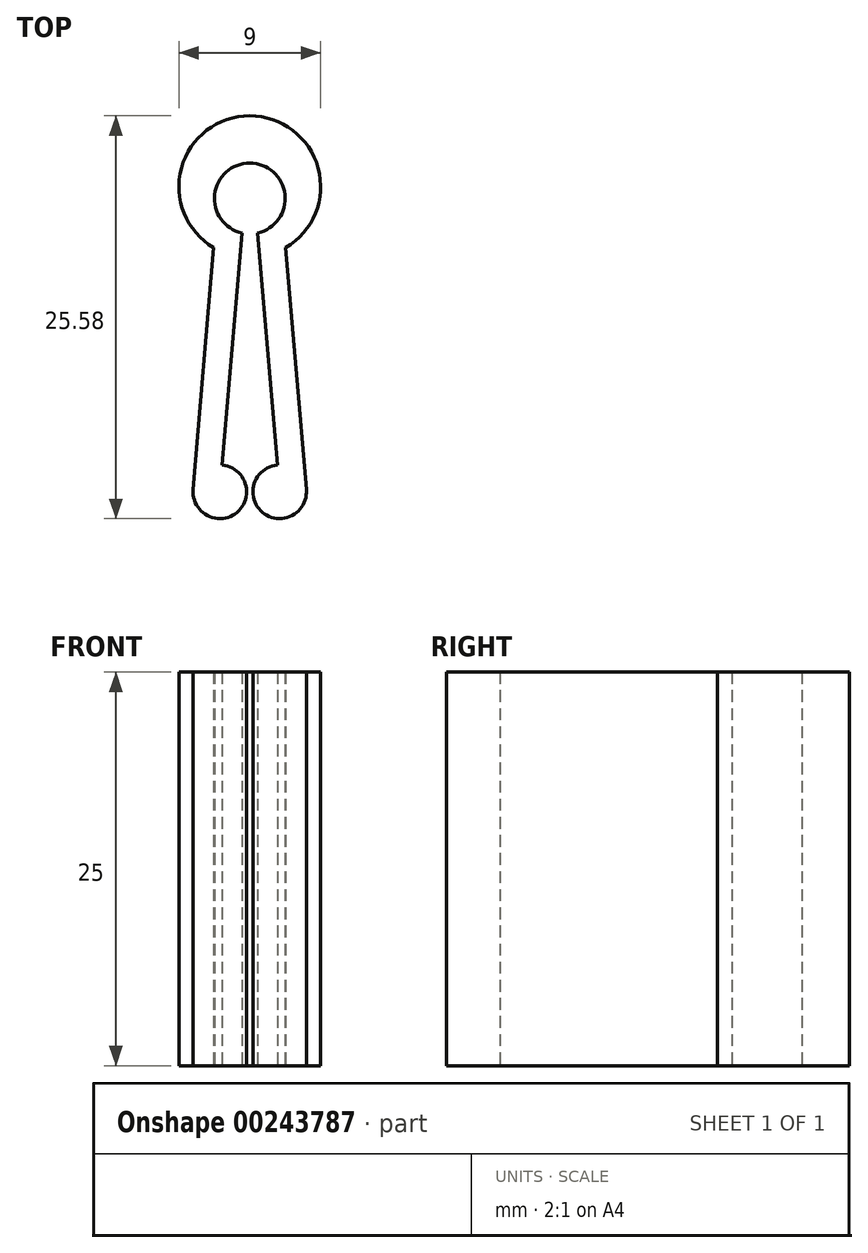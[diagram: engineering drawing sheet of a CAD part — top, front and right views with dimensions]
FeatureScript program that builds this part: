
annotation { "Feature Type Name" : "Feature", "Feature Type Description" : "" }
export const myFeature = defineFeature(function(context is Context, id is Id, definition is map)
    precondition{}
    {
        {
            var Q0;
            Q0=qCreatedBy(makeId("Top.planeOp"),FACE);
            var sketch = newSketch(context, id + "F0", { "sketchPlane" : qUnion([Q0])});
            skArc(sketch, "E0", {"start": v(0.5, 18) * mm, "mid": v(0, 22.44) * mm, "end": v(-0.5, 18) * mm});
            skLineSegment(sketch, "E1", {"start": v(0.5, 18) * mm, "end": v(1.76, 3.25) * mm});
            skLineSegment(sketch, "E2", {"start": v(-0.5, 18) * mm, "end": v(-1.76, 3.25) * mm});
            skArc(sketch, "E3", {"start": v(1.76, 3.25) * mm, "mid": v(0.8, 0.26) * mm, "end": v(3.6, 1.7) * mm});
            skArc(sketch, "E4", {"start": v(-3.6, 1.7) * mm, "mid": v(-0.8, 0.26) * mm, "end": v(-1.76, 3.25) * mm});
            skArc(sketch, "E5", {"start": v(2.29, 17.07) * mm, "mid": v(0, 25.44) * mm, "end": v(-2.29, 17.07) * mm});
            skLineSegment(sketch, "E6", {"start": v(3.6, 1.7) * mm, "end": v(2.29, 17.07) * mm});
            skLineSegment(sketch, "E7", {"start": v(-2.29, 17.07) * mm, "end": v(-3.6, 1.7) * mm});
            skSolve(sketch);
        }
        {
            var Q0;
            Q0=makeQuery(id+"F0.imprint","IMPRINT",FACE,{"disambiguationData":[TD([[makeQuery(id+"F0.imprint","IMPRINT",EDGE,{"derivedFrom":sQuery(id+"F0.wireOp",EDGE,"E0")}),-1.0]])]});
            extrude(context, id + "F1", {"entities" : qUnion([Q0]), "depth" : 25 * mm});
        }
    });
